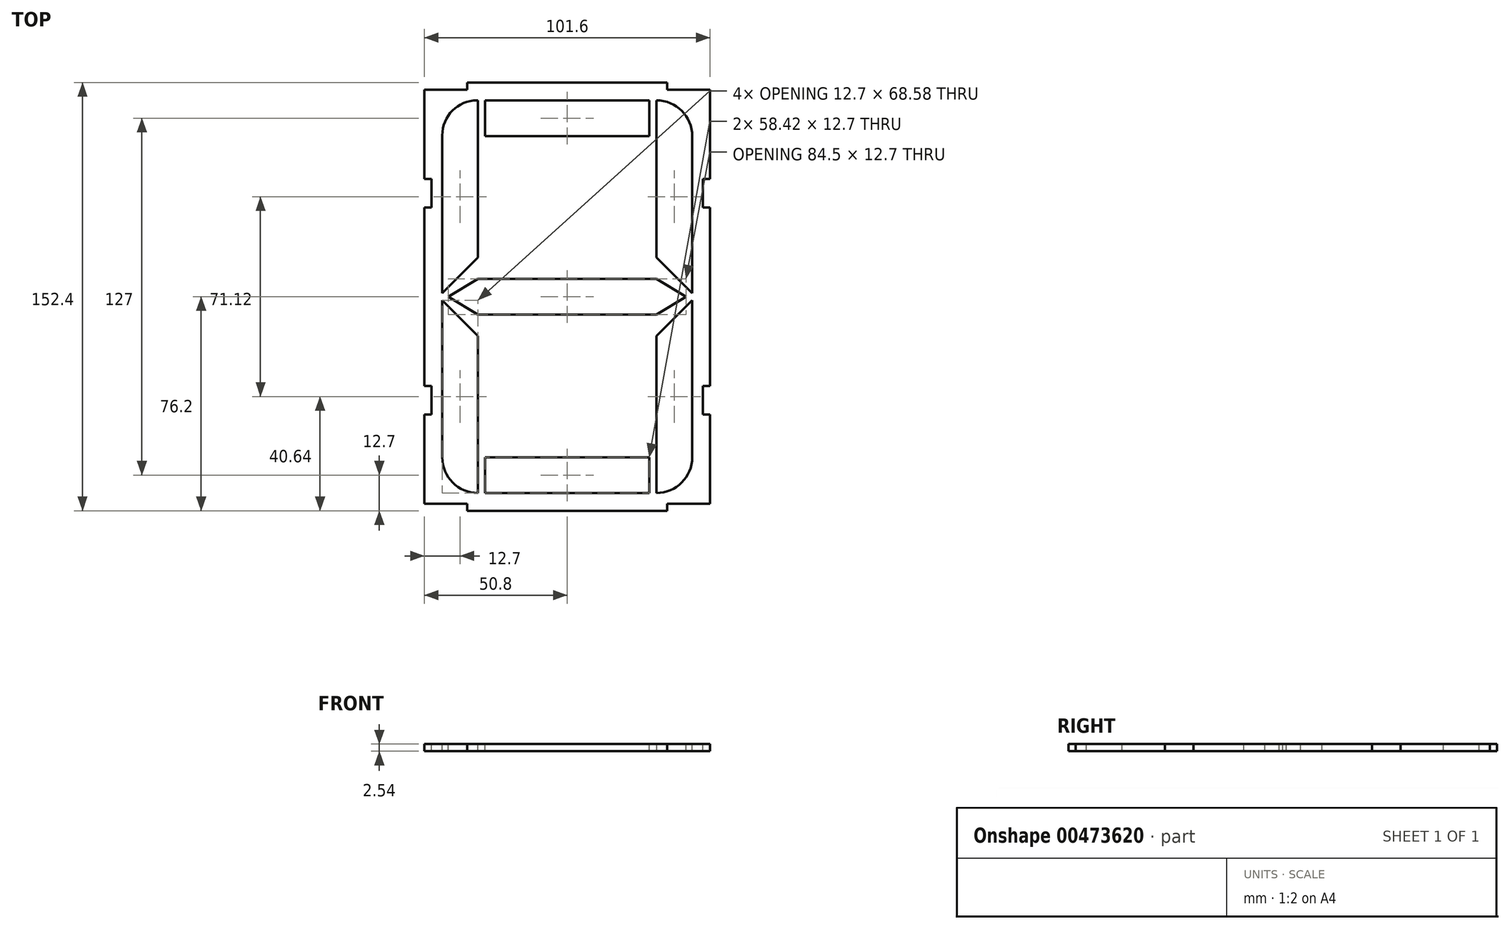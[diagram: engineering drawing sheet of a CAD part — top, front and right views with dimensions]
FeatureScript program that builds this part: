
annotation { "Feature Type Name" : "Feature", "Feature Type Description" : "" }
export const myFeature = defineFeature(function(context is Context, id is Id, definition is map)
    precondition{}
    {
        {
            var Q0;
            Q0=qCreatedBy(makeId("Top.planeOp"),FACE);
            var sketch = newSketch(context, id + "F0", { "sketchPlane" : qUnion([Q0])});
            skLineSegment(sketch, "E0.bottom", {"start": v(50.8, 76.2) * mm, "end": v(-50.8, 76.2) * mm});
            skLineSegment(sketch, "E0.top", {"start": v(50.8, -76.2) * mm, "end": v(-50.8, -76.2) * mm});
            skLineSegment(sketch, "E0.left", {"start": v(50.8, 76.2) * mm, "end": v(50.8, -76.2) * mm});
            skLineSegment(sketch, "E0.right", {"start": v(-50.8, 76.2) * mm, "end": v(-50.8, -76.2) * mm});
            skPoint(sketch, "E0.middle", {"position": v(0, 0) * mm});
            skSolve(sketch);
        }
        {
            var Q0;
            Q0=makeQuery(id+"F0.imprint","IMPRINT",FACE,{"disambiguationData":[TD([[makeQuery(id+"F0.imprint","IMPRINT",EDGE,{"derivedFrom":sQuery(id+"F0.wireOp",EDGE,"E0.bottom")}),1.0]])]});
            extrude(context, id + "F1", {"entities" : qUnion([Q0]), "depth" : 2.54 * mm});
        }
        {
            var Q0;
            Q0=makeQuery(id+"F1.opExtrude","CAP_FACE",FACE,{"disambiguationData":[OSD([sQuery(id+"F0.wireOp",EDGE,"E0.bottom"),sQuery(id+"F0.wireOp",EDGE,"E0.top"),sQuery(id+"F0.wireOp",EDGE,"E0.left"),sQuery(id+"F0.wireOp",EDGE,"E0.right")])],"isStart":false});
            var sketch = newSketch(context, id + "F2", { "sketchPlane" : qUnion([Q0])});
            skLineSegment(sketch, "E1.bottom", {"start": v(-44.45, 69.85) * mm, "end": v(-31.75, 69.85) * mm});
            skLineSegment(sketch, "E1.top", {"start": v(-44.45, 1.27) * mm, "end": v(-31.75, 1.27) * mm});
            skLineSegment(sketch, "E1.left", {"start": v(-44.45, 69.85) * mm, "end": v(-44.45, 1.27) * mm});
            skLineSegment(sketch, "E1.right", {"start": v(-31.75, 69.85) * mm, "end": v(-31.75, 1.27) * mm});
            skSolve(sketch);
        }
        {
            var Q0;
            Q0=makeQuery(id+"F2.imprint","IMPRINT",FACE,{"disambiguationData":[TD([[makeQuery(id+"F2.imprint","IMPRINT",EDGE,{"derivedFrom":sQuery(id+"F2.wireOp",EDGE,"E1.bottom")}),-1.0]])]});
            extrude(context, id + "F3", {"entities" : qUnion([Q0]), "operationType" : NewBodyOperationType.REMOVE, "endBound" : BoundingType.THROUGH_ALL, "oppositeDirection" : true, "depth" : 25.4 * mm});
        }
        {
            var Q0;
            Q0=makeQuery(id+"F3.boolean.opBoolean","COPY",EDGE,{"derivedFrom":makeQuery(id+"F3.opExtrude","SWEPT_EDGE",EDGE,{"disambiguationData":[OSD([sQuery(id+"F2.wireOp",EDGE,"E1.top"),sQuery(id+"F2.wireOp",EDGE,"E1.right")])]})});
            chamfer(context, id + "F4", {"entities" : qUnion([Q0]), "chamferType" : ChamferType.OFFSET_ANGLE, "width" : 12.7 * mm, "oppositeDirection" : false, "angle" : 45 * degree, "tangentPropagation" : true});
        }
        {
            var Q0;
            Q0=makeQuery(id+"F3.boolean.opBoolean","COPY",EDGE,{"derivedFrom":makeQuery(id+"F3.opExtrude","SWEPT_EDGE",EDGE,{"disambiguationData":[OSD([sQuery(id+"F2.wireOp",EDGE,"E1.bottom"),sQuery(id+"F2.wireOp",EDGE,"E1.left")])]})});
            fillet(context, id + "F5", {"entities" : qUnion([Q0]), "radius" : 12.45 * mm, "tangentPropagation" : true, "allowEdgeOverflow" : false});
        }
        {
            var Q0;
            Q0=makeQuery(id+"F1.opExtrude","CAP_FACE",FACE,{"disambiguationData":[OSD([sQuery(id+"F0.wireOp",EDGE,"E0.bottom"),sQuery(id+"F0.wireOp",EDGE,"E0.top"),sQuery(id+"F0.wireOp",EDGE,"E0.left"),sQuery(id+"F0.wireOp",EDGE,"E0.right")])],"isStart":false});
            var sketch = newSketch(context, id + "F6", { "sketchPlane" : qUnion([Q0])});
            skLineSegment(sketch, "E2.bottom", {"start": v(-29.21, 69.85) * mm, "end": v(29.2, 69.85) * mm});
            skLineSegment(sketch, "E2.top", {"start": v(-29.21, 57.15) * mm, "end": v(29.2, 57.15) * mm});
            skLineSegment(sketch, "E2.left", {"start": v(-29.21, 69.85) * mm, "end": v(-29.21, 57.15) * mm});
            skLineSegment(sketch, "E2.right", {"start": v(29.2, 69.85) * mm, "end": v(29.2, 57.15) * mm});
            skSolve(sketch);
        }
        {
            var Q0;
            Q0=makeQuery(id+"F6.imprint","IMPRINT",FACE,{"disambiguationData":[TD([[makeQuery(id+"F6.imprint","IMPRINT",EDGE,{"derivedFrom":sQuery(id+"F6.wireOp",EDGE,"E2.bottom")}),-1.0]])]});
            extrude(context, id + "F7", {"entities" : qUnion([Q0]), "operationType" : NewBodyOperationType.REMOVE, "endBound" : BoundingType.THROUGH_ALL, "oppositeDirection" : true, "depth" : 25.4 * mm});
        }
        {
            var Q0;
            Q0=makeQuery(id+"F1.opExtrude","CAP_FACE",FACE,{"disambiguationData":[OSD([sQuery(id+"F0.wireOp",EDGE,"E0.bottom"),sQuery(id+"F0.wireOp",EDGE,"E0.top"),sQuery(id+"F0.wireOp",EDGE,"E0.left"),sQuery(id+"F0.wireOp",EDGE,"E0.right")])],"isStart":false});
            var sketch = newSketch(context, id + "F8", { "sketchPlane" : qUnion([Q0])});
            skLineSegment(sketch, "E3.bottom", {"start": v(31.75, 69.85) * mm, "end": v(44.45, 69.85) * mm});
            skLineSegment(sketch, "E3.top", {"start": v(31.75, 1.27) * mm, "end": v(44.45, 1.27) * mm});
            skLineSegment(sketch, "E3.left", {"start": v(31.75, 69.85) * mm, "end": v(31.75, 1.27) * mm});
            skLineSegment(sketch, "E3.right", {"start": v(44.45, 69.85) * mm, "end": v(44.45, 1.27) * mm});
            skSolve(sketch);
        }
        {
            var Q0;
            Q0=makeQuery(id+"F8.imprint","IMPRINT",FACE,{"disambiguationData":[TD([[makeQuery(id+"F8.imprint","IMPRINT",EDGE,{"derivedFrom":sQuery(id+"F8.wireOp",EDGE,"E3.bottom")}),-1.0]])]});
            extrude(context, id + "F9", {"entities" : qUnion([Q0]), "operationType" : NewBodyOperationType.REMOVE, "endBound" : BoundingType.THROUGH_ALL, "oppositeDirection" : true, "depth" : 25.4 * mm});
        }
        {
            var Q0;
            Q0=makeQuery(id+"F9.boolean.opBoolean","COPY",EDGE,{"derivedFrom":makeQuery(id+"F9.opExtrude","SWEPT_EDGE",EDGE,{"disambiguationData":[OSD([sQuery(id+"F8.wireOp",EDGE,"E3.bottom"),sQuery(id+"F8.wireOp",EDGE,"E3.right")])]})});
            fillet(context, id + "F10", {"entities" : qUnion([Q0]), "radius" : 12.7 * mm, "tangentPropagation" : true, "allowEdgeOverflow" : false});
        }
        {
            var Q0;
            Q0=makeQuery(id+"F9.boolean.opBoolean","COPY",EDGE,{"derivedFrom":makeQuery(id+"F9.opExtrude","SWEPT_EDGE",EDGE,{"disambiguationData":[OSD([sQuery(id+"F8.wireOp",EDGE,"E3.top"),sQuery(id+"F8.wireOp",EDGE,"E3.left")])]})});
            chamfer(context, id + "F11", {"entities" : qUnion([Q0]), "chamferType" : ChamferType.OFFSET_ANGLE, "width" : 12.7 * mm, "oppositeDirection" : false, "angle" : 45 * degree, "tangentPropagation" : true});
        }
        {
            var Q0;
            Q0=makeQuery(id+"F1.opExtrude","CAP_FACE",FACE,{"disambiguationData":[OSD([sQuery(id+"F0.wireOp",EDGE,"E0.bottom"),sQuery(id+"F0.wireOp",EDGE,"E0.top"),sQuery(id+"F0.wireOp",EDGE,"E0.left"),sQuery(id+"F0.wireOp",EDGE,"E0.right")])],"isStart":false});
            var sketch = newSketch(context, id + "F12", { "sketchPlane" : qUnion([Q0])});
            skLineSegment(sketch, "E4.bottom", {"start": v(-44.45, -1.27) * mm, "end": v(-31.75, -1.27) * mm});
            skLineSegment(sketch, "E4.top", {"start": v(-44.45, -69.85) * mm, "end": v(-31.75, -69.85) * mm});
            skLineSegment(sketch, "E4.left", {"start": v(-44.45, -1.27) * mm, "end": v(-44.45, -69.85) * mm});
            skLineSegment(sketch, "E4.right", {"start": v(-31.75, -1.27) * mm, "end": v(-31.75, -69.85) * mm});
            skSolve(sketch);
        }
        {
            var Q0;
            Q0=makeQuery(id+"F12.imprint","IMPRINT",FACE,{"disambiguationData":[TD([[makeQuery(id+"F12.imprint","IMPRINT",EDGE,{"derivedFrom":sQuery(id+"F12.wireOp",EDGE,"E4.bottom")}),-1.0]])]});
            extrude(context, id + "F13", {"entities" : qUnion([Q0]), "operationType" : NewBodyOperationType.REMOVE, "endBound" : BoundingType.THROUGH_ALL, "oppositeDirection" : true, "depth" : 25.4 * mm});
        }
        {
            var Q0;
            Q0=makeQuery(id+"F13.boolean.opBoolean","COPY",EDGE,{"derivedFrom":makeQuery(id+"F13.opExtrude","SWEPT_EDGE",EDGE,{"disambiguationData":[OSD([sQuery(id+"F12.wireOp",EDGE,"E4.bottom"),sQuery(id+"F12.wireOp",EDGE,"E4.right")])]})});
            chamfer(context, id + "F14", {"entities" : qUnion([Q0]), "chamferType" : ChamferType.OFFSET_ANGLE, "width" : 12.7 * mm, "oppositeDirection" : false, "angle" : 45 * degree, "tangentPropagation" : true});
        }
        {
            var Q0;
            Q0=makeQuery(id+"F13.boolean.opBoolean","COPY",EDGE,{"derivedFrom":makeQuery(id+"F13.opExtrude","SWEPT_EDGE",EDGE,{"disambiguationData":[OSD([sQuery(id+"F12.wireOp",EDGE,"E4.top"),sQuery(id+"F12.wireOp",EDGE,"E4.left")])]})});
            fillet(context, id + "F15", {"entities" : qUnion([Q0]), "radius" : 12.7 * mm, "tangentPropagation" : true, "allowEdgeOverflow" : false});
        }
        {
            var Q0;
            Q0=makeQuery(id+"F1.opExtrude","CAP_FACE",FACE,{"disambiguationData":[OSD([sQuery(id+"F0.wireOp",EDGE,"E0.bottom"),sQuery(id+"F0.wireOp",EDGE,"E0.top"),sQuery(id+"F0.wireOp",EDGE,"E0.left"),sQuery(id+"F0.wireOp",EDGE,"E0.right")])],"isStart":false});
            var sketch = newSketch(context, id + "F16", { "sketchPlane" : qUnion([Q0])});
            skLineSegment(sketch, "E5.bottom", {"start": v(44.45, -1.27) * mm, "end": v(31.75, -1.27) * mm});
            skLineSegment(sketch, "E5.top", {"start": v(44.45, -69.85) * mm, "end": v(31.75, -69.85) * mm});
            skLineSegment(sketch, "E5.left", {"start": v(44.45, -1.27) * mm, "end": v(44.45, -69.85) * mm});
            skLineSegment(sketch, "E5.right", {"start": v(31.75, -1.27) * mm, "end": v(31.75, -69.85) * mm});
            skSolve(sketch);
        }
        {
            var Q0;
            Q0=makeQuery(id+"F16.imprint","IMPRINT",FACE,{"disambiguationData":[TD([[makeQuery(id+"F16.imprint","IMPRINT",EDGE,{"derivedFrom":sQuery(id+"F16.wireOp",EDGE,"E5.bottom")}),1.0]])]});
            extrude(context, id + "F17", {"entities" : qUnion([Q0]), "operationType" : NewBodyOperationType.REMOVE, "endBound" : BoundingType.THROUGH_ALL, "oppositeDirection" : true, "depth" : 25.4 * mm});
        }
        {
            var Q0;
            Q0=makeQuery(id+"F17.boolean.opBoolean","COPY",EDGE,{"derivedFrom":makeQuery(id+"F17.opExtrude","SWEPT_EDGE",EDGE,{"disambiguationData":[OSD([sQuery(id+"F16.wireOp",EDGE,"E5.bottom"),sQuery(id+"F16.wireOp",EDGE,"E5.right")])]})});
            chamfer(context, id + "F18", {"entities" : qUnion([Q0]), "chamferType" : ChamferType.OFFSET_ANGLE, "width" : 12.7 * mm, "oppositeDirection" : false, "angle" : 45 * degree, "tangentPropagation" : true});
        }
        {
            var Q0;
            Q0=makeQuery(id+"F17.boolean.opBoolean","COPY",EDGE,{"derivedFrom":makeQuery(id+"F17.opExtrude","SWEPT_EDGE",EDGE,{"disambiguationData":[OSD([sQuery(id+"F16.wireOp",EDGE,"E5.top"),sQuery(id+"F16.wireOp",EDGE,"E5.left")])]})});
            fillet(context, id + "F19", {"entities" : qUnion([Q0]), "radius" : 12.7 * mm, "tangentPropagation" : true, "allowEdgeOverflow" : false});
        }
        {
            var Q0;
            Q0=makeQuery(id+"F1.opExtrude","CAP_FACE",FACE,{"disambiguationData":[OSD([sQuery(id+"F0.wireOp",EDGE,"E0.bottom"),sQuery(id+"F0.wireOp",EDGE,"E0.top"),sQuery(id+"F0.wireOp",EDGE,"E0.left"),sQuery(id+"F0.wireOp",EDGE,"E0.right")])],"isStart":false});
            var sketch = newSketch(context, id + "F20", { "sketchPlane" : qUnion([Q0])});
            skLineSegment(sketch, "E6.bottom", {"start": v(-29.21, -69.85) * mm, "end": v(29.2, -69.85) * mm});
            skLineSegment(sketch, "E6.top", {"start": v(-29.21, -57.15) * mm, "end": v(29.2, -57.15) * mm});
            skLineSegment(sketch, "E6.left", {"start": v(-29.21, -69.85) * mm, "end": v(-29.21, -57.15) * mm});
            skLineSegment(sketch, "E6.right", {"start": v(29.2, -69.85) * mm, "end": v(29.2, -57.15) * mm});
            skSolve(sketch);
        }
        {
            var Q0;
            Q0=makeQuery(id+"F20.imprint","IMPRINT",FACE,{"disambiguationData":[TD([[makeQuery(id+"F20.imprint","IMPRINT",EDGE,{"derivedFrom":sQuery(id+"F20.wireOp",EDGE,"E6.bottom")}),1.0]])]});
            extrude(context, id + "F21", {"entities" : qUnion([Q0]), "operationType" : NewBodyOperationType.REMOVE, "endBound" : BoundingType.THROUGH_ALL, "oppositeDirection" : true, "depth" : 25.4 * mm});
        }
        {
            var Q0;
            Q0=makeQuery(id+"F1.opExtrude","CAP_FACE",FACE,{"disambiguationData":[OSD([sQuery(id+"F0.wireOp",EDGE,"E0.bottom"),sQuery(id+"F0.wireOp",EDGE,"E0.top"),sQuery(id+"F0.wireOp",EDGE,"E0.left"),sQuery(id+"F0.wireOp",EDGE,"E0.right")])],"isStart":false});
            var sketch = newSketch(context, id + "F22", { "sketchPlane" : qUnion([Q0])});
            skLineSegment(sketch, "E7", {"start": v(-42.25, 0) * mm, "end": v(-31.75, 6.35) * mm});
            skLineSegment(sketch, "E8", {"start": v(-31.75, 6.35) * mm, "end": v(31.75, 6.35) * mm});
            skLineSegment(sketch, "E9", {"start": v(31.75, 6.35) * mm, "end": v(42.25, 0) * mm});
            skLineSegment(sketch, "E10", {"start": v(42.25, 0) * mm, "end": v(31.75, -6.35) * mm});
            skLineSegment(sketch, "E11", {"start": v(31.75, -6.35) * mm, "end": v(-31.75, -6.35) * mm});
            skLineSegment(sketch, "E12", {"start": v(-31.75, -6.35) * mm, "end": v(-42.25, 0) * mm});
            skLineSegment(sketch, "E13", {"start": v(-42.25, 0) * mm, "end": v(-16.2, 0) * mm, "construction": true});
            skSolve(sketch);
        }
        {
            var Q0;
            Q0=makeQuery(id+"F22.imprint","IMPRINT",FACE,{"disambiguationData":[TD([[makeQuery(id+"F22.imprint","IMPRINT",EDGE,{"derivedFrom":sQuery(id+"F22.wireOp",EDGE,"E7")}),-1.0]])]});
            extrude(context, id + "F23", {"entities" : qUnion([Q0]), "operationType" : NewBodyOperationType.REMOVE, "oppositeDirection" : true, "depth" : 25.4 * mm});
        }
        {
            var Q0;
            Q0=makeQuery(id+"F1.opExtrude","CAP_FACE",FACE,{"disambiguationData":[OSD([sQuery(id+"F0.wireOp",EDGE,"E0.bottom"),sQuery(id+"F0.wireOp",EDGE,"E0.top"),sQuery(id+"F0.wireOp",EDGE,"E0.left"),sQuery(id+"F0.wireOp",EDGE,"E0.right")])],"isStart":false});
            var sketch = newSketch(context, id + "F24", { "sketchPlane" : qUnion([Q0])});
            skLineSegment(sketch, "E14", {"start": v(-39.37, -76.2) * mm, "end": v(-41.91, -73.66) * mm});
            skLineSegment(sketch, "E15", {"start": v(-41.91, -73.66) * mm, "end": v(-50.8, -73.66) * mm});
            skLineSegment(sketch, "E16", {"start": v(-50.8, -73.66) * mm, "end": v(-50.8, -76.2) * mm});
            skLineSegment(sketch, "E17", {"start": v(-50.8, -76.2) * mm, "end": v(-39.37, -76.2) * mm});
            skLineSegment(sketch, "E18", {"start": v(39.37, -76.2) * mm, "end": v(41.91, -73.66) * mm});
            skLineSegment(sketch, "E19", {"start": v(41.91, -73.66) * mm, "end": v(50.8, -73.66) * mm});
            skLineSegment(sketch, "E20", {"start": v(50.8, -73.66) * mm, "end": v(50.8, -76.2) * mm});
            skLineSegment(sketch, "E21", {"start": v(50.8, -76.2) * mm, "end": v(39.37, -76.2) * mm});
            skSolve(sketch);
        }
        {
            var Q0;
            Q0=makeQuery(id+"F24.imprint","IMPRINT",FACE,{"disambiguationData":[TD([[makeQuery(id+"F24.imprint","IMPRINT",EDGE,{"derivedFrom":sQuery(id+"F24.wireOp",EDGE,"E14")}),1.0]])]});
            var Q1;
            Q1=makeQuery(id+"F24.imprint","IMPRINT",FACE,{"disambiguationData":[TD([[makeQuery(id+"F24.imprint","IMPRINT",EDGE,{"derivedFrom":sQuery(id+"F24.wireOp",EDGE,"E18")}),-1.0]])]});
            extrude(context, id + "F25", {"entities" : qUnion([Q0, Q1]), "operationType" : NewBodyOperationType.REMOVE, "oppositeDirection" : true, "depth" : 25.4 * mm});
        }
        {
            var Q0;
            Q0=makeQuery(id+"F1.opExtrude","CAP_FACE",FACE,{"disambiguationData":[OSD([sQuery(id+"F0.wireOp",EDGE,"E0.bottom"),sQuery(id+"F0.wireOp",EDGE,"E0.top"),sQuery(id+"F0.wireOp",EDGE,"E0.left"),sQuery(id+"F0.wireOp",EDGE,"E0.right")])],"isStart":false});
            var sketch = newSketch(context, id + "F26", { "sketchPlane" : qUnion([Q0])});
            skLineSegment(sketch, "E22", {"start": v(-50.8, 76.2) * mm, "end": v(-39.37, 76.2) * mm});
            skLineSegment(sketch, "E23", {"start": v(-39.37, 76.2) * mm, "end": v(-41.91, 73.66) * mm});
            skLineSegment(sketch, "E24", {"start": v(-41.91, 73.66) * mm, "end": v(-50.8, 73.66) * mm});
            skLineSegment(sketch, "E25", {"start": v(-50.8, 73.66) * mm, "end": v(-50.8, 76.2) * mm});
            skLineSegment(sketch, "E26", {"start": v(39.37, 76.2) * mm, "end": v(41.9, 73.66) * mm});
            skLineSegment(sketch, "E27", {"start": v(41.9, 73.66) * mm, "end": v(50.8, 73.66) * mm});
            skLineSegment(sketch, "E28", {"start": v(50.8, 73.66) * mm, "end": v(50.8, 76.2) * mm});
            skLineSegment(sketch, "E29", {"start": v(50.8, 76.2) * mm, "end": v(39.37, 76.2) * mm});
            skSolve(sketch);
        }
        {
            var Q0;
            Q0=makeQuery(id+"F26.imprint","IMPRINT",FACE,{"disambiguationData":[TD([[makeQuery(id+"F26.imprint","IMPRINT",EDGE,{"derivedFrom":sQuery(id+"F26.wireOp",EDGE,"E22")}),1.0]])]});
            var Q1;
            Q1=makeQuery(id+"F26.imprint","IMPRINT",FACE,{"disambiguationData":[TD([[makeQuery(id+"F26.imprint","IMPRINT",EDGE,{"derivedFrom":sQuery(id+"F26.wireOp",EDGE,"E26")}),1.0]])]});
            extrude(context, id + "F27", {"entities" : qUnion([Q0, Q1]), "operationType" : NewBodyOperationType.REMOVE, "oppositeDirection" : true, "depth" : 25.4 * mm});
        }
        {
            var Q0;
            Q0=makeQuery(id+"F1.opExtrude","CAP_FACE",FACE,{"disambiguationData":[OSD([sQuery(id+"F0.wireOp",EDGE,"E0.bottom"),sQuery(id+"F0.wireOp",EDGE,"E0.top"),sQuery(id+"F0.wireOp",EDGE,"E0.left"),sQuery(id+"F0.wireOp",EDGE,"E0.right")])],"isStart":false});
            var sketch = newSketch(context, id + "F28", { "sketchPlane" : qUnion([Q0])});
            skLineSegment(sketch, "E30", {"start": v(50.8, 41.91) * mm, "end": v(48.26, 41.91) * mm});
            skLineSegment(sketch, "E31", {"start": v(48.26, 41.91) * mm, "end": v(48.26, 31.75) * mm});
            skLineSegment(sketch, "E32", {"start": v(48.26, 31.75) * mm, "end": v(50.8, 31.75) * mm});
            skLineSegment(sketch, "E33", {"start": v(50.8, 31.75) * mm, "end": v(50.8, -31.75) * mm});
            skLineSegment(sketch, "E34", {"start": v(50.8, -31.75) * mm, "end": v(48.26, -31.75) * mm});
            skLineSegment(sketch, "E35", {"start": v(48.26, -31.75) * mm, "end": v(48.26, -41.9) * mm});
            skLineSegment(sketch, "E36", {"start": v(48.26, -41.9) * mm, "end": v(50.8, -41.9) * mm});
            skLineSegment(sketch, "E37", {"start": v(50.8, -41.9) * mm, "end": v(50.8, -31.75) * mm});
            skLineSegment(sketch, "E38", {"start": v(50.8, 31.75) * mm, "end": v(50.8, 41.91) * mm});
            skSolve(sketch);
        }
        {
            var Q0;
            Q0 = qSketchRegion(id + "F28", true);
            extrude(context, id + "F29", {"entities" : qUnion([Q0]), "operationType" : NewBodyOperationType.REMOVE, "oppositeDirection" : true, "depth" : 25.4 * mm});
        }
        {
            var Q0;
            Q0=makeQuery(id+"F1.opExtrude","CAP_FACE",FACE,{"disambiguationData":[OSD([sQuery(id+"F0.wireOp",EDGE,"E0.bottom"),sQuery(id+"F0.wireOp",EDGE,"E0.top"),sQuery(id+"F0.wireOp",EDGE,"E0.left"),sQuery(id+"F0.wireOp",EDGE,"E0.right")])],"isStart":false});
            var sketch = newSketch(context, id + "F30", { "sketchPlane" : qUnion([Q0])});
            skLineSegment(sketch, "E39", {"start": v(-50.8, 41.9) * mm, "end": v(-50.8, 31.75) * mm});
            skPoint(sketch, "E39.startSnap0", {"position": v(-31.75, 41.9) * mm});
            skLineSegment(sketch, "E40", {"start": v(-50.8, 31.75) * mm, "end": v(-48.26, 31.75) * mm});
            skLineSegment(sketch, "E41", {"start": v(-48.26, 31.75) * mm, "end": v(-48.26, 41.9) * mm});
            skLineSegment(sketch, "E42", {"start": v(-48.26, 41.9) * mm, "end": v(-50.8, 41.9) * mm});
            skLineSegment(sketch, "E43", {"start": v(-50.8, -31.75) * mm, "end": v(-50.8, -41.9) * mm});
            skLineSegment(sketch, "E44", {"start": v(-50.8, -41.9) * mm, "end": v(-48.26, -41.9) * mm});
            skLineSegment(sketch, "E45", {"start": v(-48.26, -41.9) * mm, "end": v(-48.26, -31.75) * mm});
            skLineSegment(sketch, "E46", {"start": v(-48.26, -31.75) * mm, "end": v(-50.8, -31.75) * mm});
            skSolve(sketch);
        }
        {
            var Q0;
            Q0 = qSketchRegion(id + "F30", true);
            extrude(context, id + "F31", {"entities" : qUnion([Q0]), "operationType" : NewBodyOperationType.REMOVE, "oppositeDirection" : true, "depth" : 25.4 * mm});
        }
        {
            var Q0;
            Q0=makeQuery(id+"F1.opExtrude","CAP_FACE",FACE,{"disambiguationData":[OSD([sQuery(id+"F0.wireOp",EDGE,"E0.bottom"),sQuery(id+"F0.wireOp",EDGE,"E0.top"),sQuery(id+"F0.wireOp",EDGE,"E0.left"),sQuery(id+"F0.wireOp",EDGE,"E0.right")])],"isStart":false});
            var sketch = newSketch(context, id + "F32", { "sketchPlane" : qUnion([Q0])});
            skLineSegment(sketch, "E47", {"start": v(-35.56, -76.2) * mm, "end": v(-50.8, -76.2) * mm});
            skLineSegment(sketch, "E48", {"start": v(-50.8, -76.2) * mm, "end": v(-50.8, -73.66) * mm});
            skLineSegment(sketch, "E49", {"start": v(-50.8, -73.66) * mm, "end": v(-35.56, -73.66) * mm});
            skLineSegment(sketch, "E50", {"start": v(-35.56, -73.66) * mm, "end": v(-35.56, -76.2) * mm});
            skLineSegment(sketch, "E51", {"start": v(50.8, -73.66) * mm, "end": v(50.8, -76.2) * mm});
            skLineSegment(sketch, "E52", {"start": v(50.8, -76.2) * mm, "end": v(35.56, -76.2) * mm});
            skLineSegment(sketch, "E53", {"start": v(35.56, -76.2) * mm, "end": v(35.56, -73.66) * mm});
            skLineSegment(sketch, "E54", {"start": v(35.56, -73.66) * mm, "end": v(50.8, -73.66) * mm});
            skLineSegment(sketch, "E55", {"start": v(-50.8, 73.66) * mm, "end": v(-50.8, 76.2) * mm});
            skLineSegment(sketch, "E56", {"start": v(-50.8, 76.2) * mm, "end": v(-35.56, 76.2) * mm});
            skLineSegment(sketch, "E57", {"start": v(-35.56, 76.2) * mm, "end": v(-35.56, 73.66) * mm});
            skPoint(sketch, "E57.endSnap0", {"position": v(-46.36, 73.66) * mm});
            skLineSegment(sketch, "E58", {"start": v(-35.56, 73.66) * mm, "end": v(-50.8, 73.66) * mm});
            skLineSegment(sketch, "E59", {"start": v(50.8, 73.66) * mm, "end": v(50.8, 76.2) * mm});
            skLineSegment(sketch, "E60", {"start": v(50.8, 76.2) * mm, "end": v(35.56, 76.2) * mm});
            skLineSegment(sketch, "E61", {"start": v(35.56, 76.2) * mm, "end": v(35.56, 73.66) * mm});
            skLineSegment(sketch, "E62", {"start": v(35.56, 73.66) * mm, "end": v(50.8, 73.66) * mm});
            skSolve(sketch);
        }
        {
            var Q0;
            Q0 = qSketchRegion(id + "F32", true);
            extrude(context, id + "F33", {"entities" : qUnion([Q0]), "operationType" : NewBodyOperationType.REMOVE, "oppositeDirection" : true, "depth" : 25.4 * mm, "offsetDistance" : 25.4 * mm});
        }
    });
